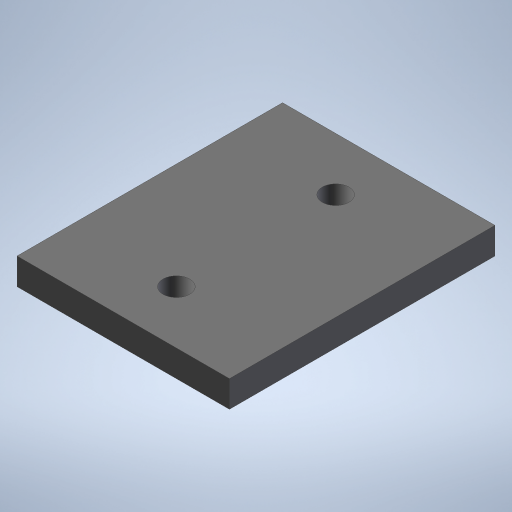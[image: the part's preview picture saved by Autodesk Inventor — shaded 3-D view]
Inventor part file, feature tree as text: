
AUTODESK INVENTOR PART (.ipt)
format: ipt  version: 2023 (Build 270158000, 158)  size: 247,808 bytes
history: native  units: mm
features: extrude x1, sketch x1
ambient origin geometry x8: Origin, YZ Plane, XZ Plane, XY Plane, X Axis, Y Axis, Z Axis, Center Point
bodies: Solid1 (feature_tree)
feature tree (2):
  extrude  "Extrusion1"  Depth=50.0mm
  sketch  "Sketch1"  dims[d0=40.0mm d1=50.0mm d2=5.0mm d3=5.0mm d4=10.0mm d5=10.0mm d6=20.0mm d7=5.0mm d8=0.0mm]
